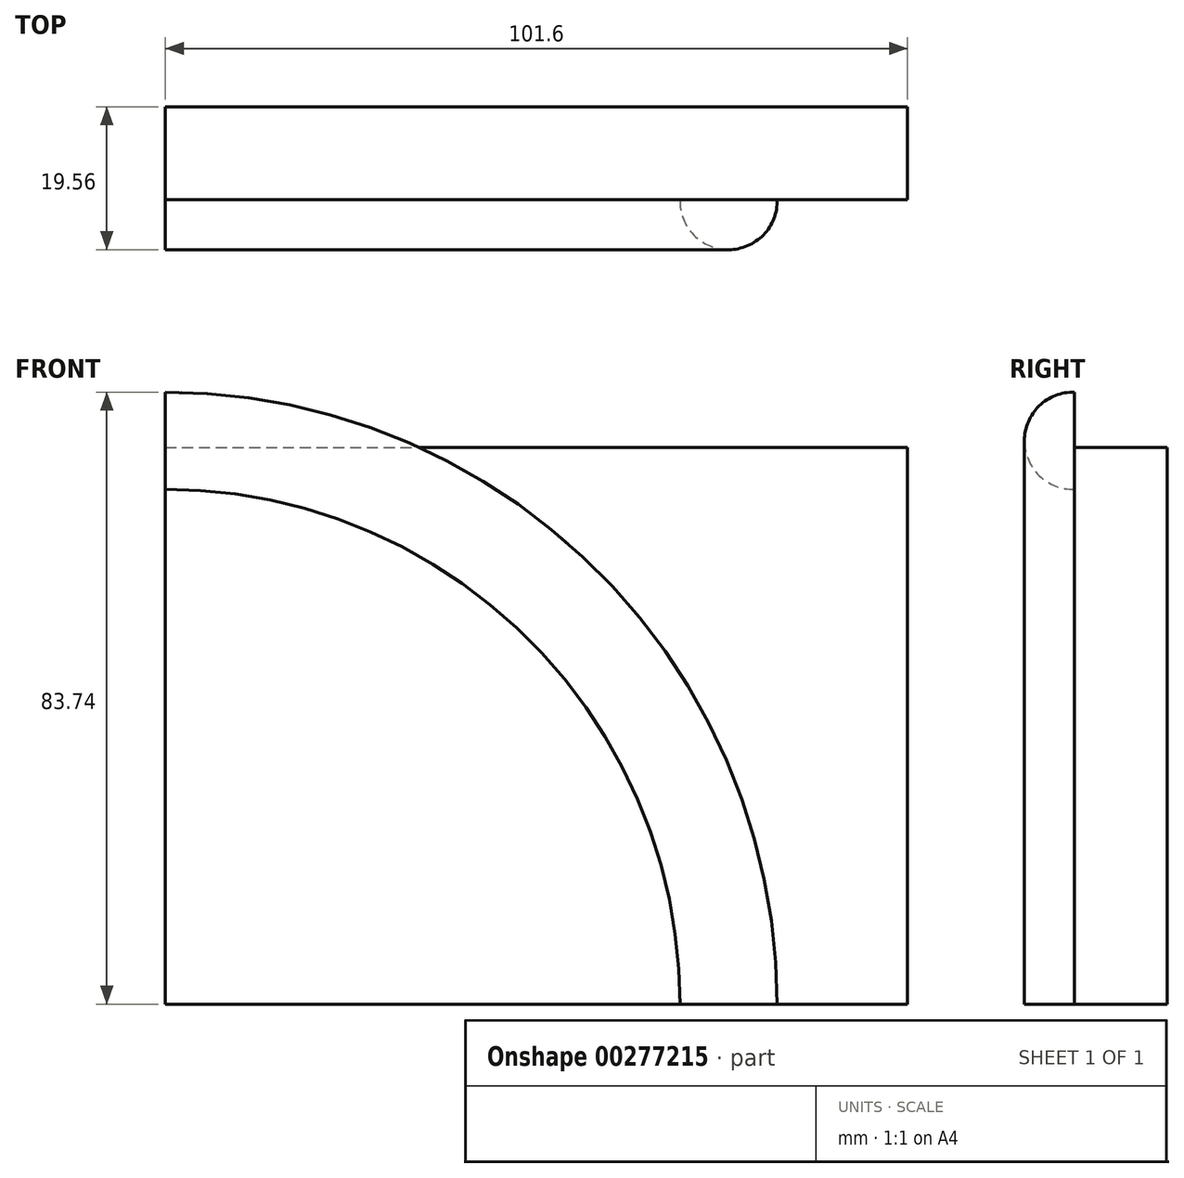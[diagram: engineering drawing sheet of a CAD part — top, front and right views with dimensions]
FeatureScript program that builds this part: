
annotation { "Feature Type Name" : "Feature", "Feature Type Description" : "" }
export const myFeature = defineFeature(function(context is Context, id is Id, definition is map)
    precondition{}
    {
        {
            var Q0;
            Q0=qCreatedBy(makeId("Front.planeOp"),FACE);
            var sketch = newSketch(context, id + "F0", { "sketchPlane" : qUnion([Q0])});
            skLineSegment(sketch, "E0.bottom", {"start": v(0, 0) * mm, "end": v(101.6, 0) * mm});
            skLineSegment(sketch, "E0.top", {"start": v(0, 76.2) * mm, "end": v(101.6, 76.2) * mm});
            skLineSegment(sketch, "E0.left", {"start": v(0, 0) * mm, "end": v(0, 76.2) * mm});
            skLineSegment(sketch, "E0.right", {"start": v(101.6, 0) * mm, "end": v(101.6, 76.2) * mm});
            skSolve(sketch);
        }
        {
            var Q0;
            Q0=makeQuery(id+"F0.imprint","IMPRINT",FACE,{"disambiguationData":[TD([[makeQuery(id+"F0.imprint","IMPRINT",EDGE,{"derivedFrom":sQuery(id+"F0.wireOp",EDGE,"E0.bottom")}),1.0]])]});
            extrude(context, id + "F1", {"entities" : qUnion([Q0]), "depth" : 12.7 * mm});
        }
        {
            var Q0;
            Q0=makeQuery(id+"F1.opExtrude","CAP_FACE",FACE,{"disambiguationData":[OSD([sQuery(id+"F0.wireOp",EDGE,"E0.bottom"),sQuery(id+"F0.wireOp",EDGE,"E0.top"),sQuery(id+"F0.wireOp",EDGE,"E0.left"),sQuery(id+"F0.wireOp",EDGE,"E0.right")])],"isStart":false});
            var sketch = newSketch(context, id + "F2", { "sketchPlane" : qUnion([Q0])});
            skArc(sketch, "E1", {"start": v(0, 76.2) * mm, "mid": v(53.88, 53.88) * mm, "end": v(76.2, 0) * mm});
            skSolve(sketch);
        }
        {
            var Q0;
            Q0=makeQuery(id+"F1.opExtrude","SWEPT_FACE",FACE,{"disambiguationData":[OSD([sQuery(id+"F0.wireOp",EDGE,"E0.bottom")])]});
            var sketch = newSketch(context, id + "F3", { "sketchPlane" : qUnion([Q0])});
            skArc(sketch, "E2", {"start": v(83.74, 12.7) * mm, "mid": v(77.1, 19.56) * mm, "end": v(70.46, 12.7) * mm});
            skSolve(sketch);
        }
        {
            var Q0;
            {var subQ0=sQuery(id+"F3.wireOp",EDGE,"E2");Q0=makeQuery(id+"F3.imprint","IMPRINT",FACE,{"disambiguationData":[TD([[makeQuery(id+"F3.imprint","IMPRINT",EDGE,{"derivedFrom":subQ0}),1.0]])]});}
            var Q1;
            Q1=sQuery(id+"F2.wireOp",EDGE,"E1");
            sweep(context, id + "F4", {"operationType" : NewBodyOperationType.ADD, "profiles" : qUnion([Q0]), "path" : qUnion([Q1])});
        }
    });
